# Revit family: EL-SK4010L3AHTZ_()0000018574_Facebased_ver-2-0_2022________
name_source: partatom
category: 照明器具
units: mm (PartAtom-declared; Revit-internal decimal feet)

## family parameters
パーツ タイプ = 標準
ホスト = 面
ロード時にボイドで切り取り = はい
丸型コネクタ寸法 = 直径を使用
光源 = はい
共有 = いいえ
注釈の向きを維持 = いいえ
部屋計算ポイント = いいえ

## types (3) — shared parameters
Depth = 443  [stored 1.45341 ft]
Height = 134
IfcExportAs = IfcLightFixtureType
URL = https://www.mitsubishielectric.co.jp
Width = 370  [stored 1.21391 ft]
カラー フィルタ = 16777215
サービススペース = いいえ
モデル = EL-SK4010L/3 AHTZ
ランプ_全光束 = 0 lm
ランプ_定格消費電力 = 0.0 W
ランプ_電流 = 0.000 A
レンダリング時に放射形状を表示 = はい
企業コード = 118713
保守率(1)良いのコメント = 保守率良いの場合：0.83
保守率(2)普通のコメント = 保守率普通の場合：0.81
保守率(3)悪いのコメント = 保守率悪いの場合：0.77
傾斜角 = -90.00°
入力電圧1(電圧指定=1) = 100 V
入力電圧2(電圧指定=2) = 200 V
入力電圧3(電圧指定=3) = 242 V
分類コード = 40300000000000
周波数 = 0 Hz
安定器_二次電圧 = 0 V
安定器_入力電力 = 0.0 W
安定器_入力電流 = 0.000 A
安定器_定格電圧 = 0 V
定格入力電圧 = 100 V
平均演色評価数(Ra) = 85
既定の高さ = 1219
材質_カバー = <カテゴリ別>
材質_ルーバー = <カテゴリ別>
材質_反射板 = <カテゴリ別>
材質_本体 = <カテゴリ別>
極数 = 1
相 = 1
積算_科目 = 1 電灯設備
製品質量 = 0.00 kg
製造元 = 三菱電機照明株式会社
設置方法 = 埋込
調光ランプの色温度変化。 = <なし>
質量 = 0.00 kg
運転質量 = 0.00 kg
長方形の幅に沿って放射 = 370  [stored 1.21391 ft]
長方形の長さに沿って放射 = 443  [stored 1.45341 ft]
開口部寸法(奥行) = 345  [stored 1.13189 ft]
開口部寸法(幅) = 345  [stored 1.13189 ft]
電圧指定 = 1
zero-valued in all types: Clearance Back, Clearance Bottom, Clearance Front, Clearance Left, Clearance Right, Clearance Top, ランプ_定格消費効率(lm/W), ランプ_本数, 直径, 配光角, 開口部寸法(径)

## per-type parameters (varying)
| type | LED制御装置 | コンバート開始日時 | フォトメトリック Web ファイル | 入力電流1 | 入力電流2 | 入力電流3 | 固有エネルギー消費効率(lm/W) | 定格光束 | 定格入力容量 | 定格入力電流 | 定格消費電力 | 消費電力1 | 消費電力2 | 消費電力3 | 皮相負荷 |
| _連調単色_初期照度補正機能搭載なし__ | 連続調光型 | 2023年03月18日(土) 04時34分10秒037 | EL-SK4010L3AHTZ_()0000018574_________TANSYOKU_-___.ies | 0.270 A | 0.140 A | 0.120 A | 129.62963 | 3500 lm | 27 VA | 0.270 A | 27.0 W | 27.0 W | 26.6 W | 26.6 W | 27 VA |
| _段調光_初期照度補正機能搭載なし_定格_ | 一般形(LN) | 2023年03月18日(土) 04時34分13秒513 | EL-SK4010L3AHTZ_()0000002610_________DANCHO_-_TEIKAKU__.ies | 0.270 A | 0.140 A | 0.120 A | 129.62963 | 3500 lm | 27 VA | 0.270 A | 27.0 W | 27.0 W | 26.6 W | 26.6 W | 27 VA |
| _段調光_初期照度補正機能搭載なし_節電_ | 一般形(LN) | 2023年03月18日(土) 04時34分11秒818 | EL-SK4010L3AHTZ_()0000018699_________DANCHO_-_SETSUDEN__.ies | 0.190 A | 0.100 A | 0.080 A | 133.870968 | 2490 lm | 19 VA | 0.190 A | 18.6 W | 18.6 W | 18.5 W | 18.5 W | 19 VA |

note: [stored X ft] marks values corroborated as IEEE doubles in the binary element streams (Revit-internal decimal feet)
